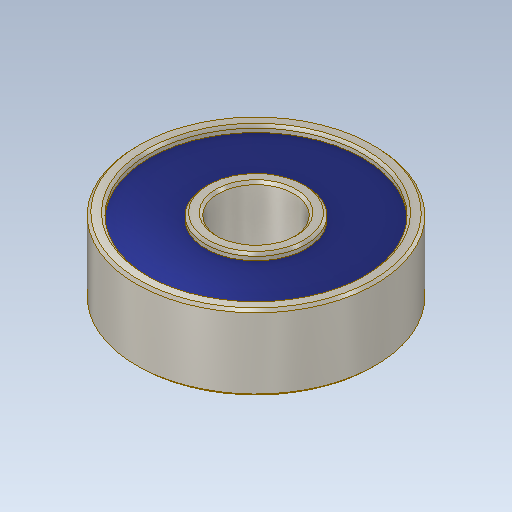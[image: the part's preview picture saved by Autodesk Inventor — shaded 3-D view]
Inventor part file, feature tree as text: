
AUTODESK INVENTOR PART (.ipt)
format: ipt  version: 2020 (Build 240168000, 168)  size: 195,584 bytes
history: native  units: mm
features: extrude x3, sketch x3, other x1, chamfer x1, projected_geometry x1
ambient origin geometry x8: Origin, YZ Plane, XZ Plane, XY Plane, X Axis, Y Axis, Z Axis, Center Point
bodies: Body1 (feature_tree)
feature tree (9):
  other  "Твердое тело1"
  extrude  "Выдавливание1"  Depth=19.0mm
  extrude  "Выдавливание2"  Depth=6.0mm
  extrude  "Выдавливание3"  Depth=6.0mm TaperAngle=0.0deg
  chamfer  "Фаска1"  Distance=1.0mm
  sketch  "Эскиз1"
  sketch  "Эскиз2"
  sketch  "Эскиз3"
  projected_geometry  "Спроецированная петля1"
